# Revit family: Automatyczny_dozownik_mydla_w_plynie_i_srodkow_dezynfekcyjnych 1 l LAB
name_source: partatom
category: Furniture
units: mm (PartAtom-declared; Revit-internal decimal feet)

## family parameters
Always vertical = Yes
Cut with Voids When Loaded = No
Host = Wall
Room Calculation Point = No
Shared = No

## types (1)
- S1000ASPB
    Depth / Glebokosc = 93 mm  [stored 0.305118 ft]
    Description = Dozownik mydła w płynie 1l LAB to niezwykle trwały naścienny podajnik mydła, wykonany ze stali nierdzewnej matowej. Jego nowoczesny design oraz najwyższa jakość wykończenia sprawiają, że idealnie nadaje się on do prestiżowych pomieszczeń. Jest łatwy w montażu i konserwacji.Duża pojemność umożliwia wygodne uzupełnianie mydła, którego ilość wewnątrz można sprawnie kontrolować dzięki przeźroczystemu owalnemu wizjerowi. Podajnik do mydła LAB wyposażony jest w bardzo solidny zamek bębenkowy. To innowacyjny i solidny dozownik.
    Height / Wysokosc = 275 mm
    Manufacturer = FANECO.com
    Manufacturer code / Kod producenta = 5901764295822
    Material = Stal nierdzewna AISI 304
    Material finish / Wykonczenie = Stal nierdzewna 304 szczotkowana
    Product code / Kod produktu = S1000ASPB
    Type Comments = Automatyczny dozownik mydła w płynie i środków dezynfekcyjnych 1 l LAB
    URL = https://faneco.com
    Weight / Waga = 1.08  kg
    Width / Szerokosc = 102 mm

note: [stored X ft] marks values corroborated as IEEE doubles in the binary element streams (Revit-internal decimal feet)

## geometry (parser evidence)
native form markers: Sweep x11
no freeform markers — native parametric forms only
